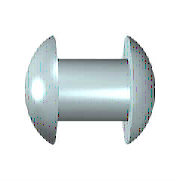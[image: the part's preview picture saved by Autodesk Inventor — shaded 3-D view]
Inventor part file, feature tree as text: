
AUTODESK INVENTOR PART (.ipt)
format: ipt  version: 2022 (Build 260153000, 153)  size: 149,504 bytes
history: native  units: mm (DEFAULTED — no unit token found)
features: sketch x1
ambient origin geometry x8: Origin, YZ Plane, XZ Plane, XY Plane, X Axis, Y Axis, Z Axis, Center Point
bodies: Solid1 (feature_tree), Body (feature_tree)
feature tree (1):
  sketch  "Sketch"  dims[d0=3.0mm d1=0.002mm d2=5.7mm d3=2.1mm d4=5.7mm d5=2.1mm d11=90.0deg d7=0.0mm d15=0.0mm d16=0.0mm]
